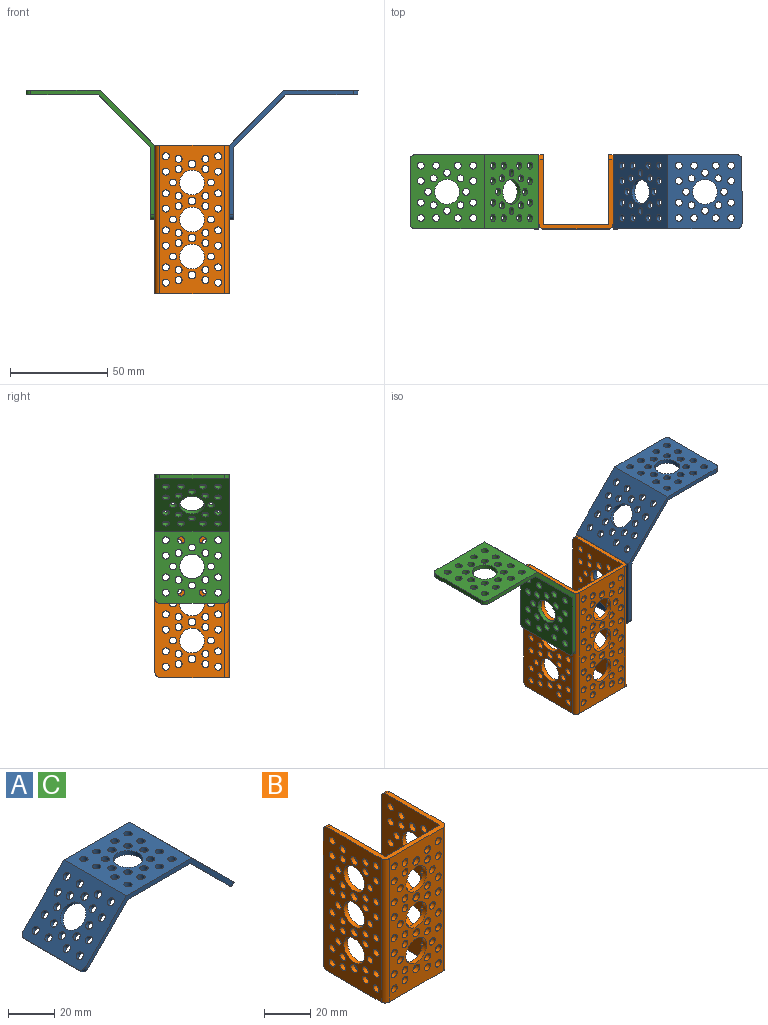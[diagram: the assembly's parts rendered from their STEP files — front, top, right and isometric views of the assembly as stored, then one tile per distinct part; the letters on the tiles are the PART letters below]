
ASSEMBLY  parts=3 mates=2
PART A: 77 faces, bbox 93.9x38.1x28.6 mm
  f0: cylinder r=1.78mm len=4.13mm, axis (-0.71,0,0.71), area 25.5mm2, adj f63,f69
  f1: cylinder r=1.78mm len=4.13mm, axis (-0.71,0,0.71), area 25.5mm2, adj f63,f69
  f2: cylinder r=1.78mm len=4.13mm, axis (-0.71,0,0.71), area 25.5mm2, adj f63,f69
  f3: cylinder r=1.78mm len=4.13mm, axis (-0.71,0,0.71), area 25.5mm2, adj f63,f69
  f4: cylinder r=1.78mm len=4.13mm, axis (-0.71,0,0.71), area 25.5mm2, adj f63,f69
  f5: cylinder r=1.78mm len=4.13mm, axis (-0.71,0,0.71), area 25.5mm2, adj f63,f69
  f6: cylinder r=1.78mm len=4.13mm, axis (-0.71,0,0.71), area 25.5mm2, adj f63,f69
  f7: cylinder r=1.78mm len=4.13mm, axis (-0.71,0,0.71), area 25.5mm2, adj f63,f69
  f8: cylinder r=1.78mm len=4.13mm, axis (0.71,0,0.71), area 25.5mm2, adj f64,f68
  f9: cylinder r=1.78mm len=4.13mm, axis (0.71,0,0.71), area 25.5mm2, adj f64,f68
  f10: cylinder r=1.78mm len=4.13mm, axis (0.71,0,0.71), area 25.5mm2, adj f64,f68
  f11: cylinder r=1.78mm len=4.13mm, axis (0.71,0,0.71), area 25.5mm2, adj f64,f68
  f12: cylinder r=1.78mm len=4.13mm, axis (0.71,0,0.71), area 25.5mm2, adj f64,f68
  f13: cylinder r=1.78mm len=4.13mm, axis (0.71,0,0.71), area 25.5mm2, adj f64,f68
  f14: cylinder r=1.78mm len=4.13mm, axis (0.71,0,0.71), area 25.5mm2, adj f64,f68
  f15: cylinder r=1.78mm len=4.13mm, axis (0.71,0,0.71), area 25.5mm2, adj f64,f68
  f16: cylinder r=1.78mm len=3.56mm, axis (0,0,-1), area 25.5mm2, adj f65,f66
  f17: cylinder r=1.78mm len=3.56mm, axis (0,0,-1), area 25.5mm2, adj f65,f66
  f18: cylinder r=1.78mm len=3.56mm, axis (0,0,-1), area 25.5mm2, adj f65,f66
  f19: cylinder r=1.78mm len=3.56mm, axis (0,0,-1), area 25.5mm2, adj f65,f66
  f20: cylinder r=1.78mm len=3.56mm, axis (0,0,-1), area 25.5mm2, adj f65,f66
  f21: cylinder r=1.78mm len=3.56mm, axis (0,0,-1), area 25.5mm2, adj f65,f66
  f22: cylinder r=1.78mm len=3.56mm, axis (0,0,-1), area 25.5mm2, adj f65,f66
  f23: cylinder r=1.78mm len=3.56mm, axis (0,0,-1), area 25.5mm2, adj f65,f66
  f24: cylinder r=1.78mm len=4.13mm, axis (-0.71,0,0.71), area 25.5mm2, adj f63,f69
  f25: cylinder r=1.78mm len=4.13mm, axis (-0.71,0,0.71), area 25.5mm2, adj f63,f69
  f26: cylinder r=1.78mm len=4.13mm, axis (-0.71,0,0.71), area 25.5mm2, adj f63,f69
  f27: cylinder r=1.78mm len=4.13mm, axis (-0.71,0,0.71), area 25.5mm2, adj f63,f69
  f28: cylinder r=1.78mm len=4.13mm, axis (0.71,0,0.71), area 25.5mm2, adj f64,f68
  f29: cylinder r=1.78mm len=4.13mm, axis (0.71,0,0.71), area 25.5mm2, adj f64,f68
  f30: cylinder r=1.78mm len=4.13mm, axis (0.71,0,0.71), area 25.5mm2, adj f64,f68
  f31: cylinder r=1.78mm len=4.13mm, axis (0.71,0,0.71), area 25.5mm2, adj f64,f68
  f32: cylinder r=1.78mm len=3.56mm, axis (0,0,-1), area 25.5mm2, adj f65,f66
  f33: cylinder r=1.78mm len=3.56mm, axis (0,0,-1), area 25.5mm2, adj f65,f66
  f34: cylinder r=1.78mm len=3.56mm, axis (0,0,-1), area 25.5mm2, adj f65,f66
  f35: cylinder r=1.78mm len=3.56mm, axis (0,0,-1), area 25.5mm2, adj f65,f66
  f36: cylinder r=1.78mm len=4.13mm, axis (0.71,0,0.71), area 25.5mm2, adj f64,f68
  f37: cylinder r=1.78mm len=4.13mm, axis (0.71,0,0.71), area 25.5mm2, adj f64,f68
  f38: cylinder r=1.78mm len=4.13mm, axis (0.71,0,0.71), area 25.5mm2, adj f64,f68
  f39: cylinder r=1.78mm len=4.13mm, axis (0.71,0,0.71), area 25.5mm2, adj f64,f68
  f40: cylinder r=1.78mm len=4.13mm, axis (0.71,0,0.71), area 25.5mm2, adj f64,f68
  f41: cylinder r=1.78mm len=4.13mm, axis (0.71,0,0.71), area 25.5mm2, adj f64,f68
  f42: cylinder r=1.78mm len=4.13mm, axis (0.71,0,0.71), area 25.5mm2, adj f64,f68
  f43: cylinder r=1.78mm len=4.13mm, axis (0.71,0,0.71), area 25.5mm2, adj f64,f68
  f44: cylinder r=1.78mm len=4.13mm, axis (-0.71,0,0.71), area 25.5mm2, adj f63,f69
  f45: cylinder r=1.78mm len=4.13mm, axis (-0.71,0,0.71), area 25.5mm2, adj f63,f69
  f46: cylinder r=1.78mm len=4.13mm, axis (-0.71,0,0.71), area 25.5mm2, adj f63,f69
  f47: cylinder r=1.78mm len=4.13mm, axis (-0.71,0,0.71), area 25.5mm2, adj f63,f69
  f48: cylinder r=1.78mm len=4.13mm, axis (-0.71,0,0.71), area 25.5mm2, adj f63,f69
  f49: cylinder r=1.78mm len=4.13mm, axis (-0.71,0,0.71), area 25.5mm2, adj f63,f69
  f50: cylinder r=1.78mm len=4.13mm, axis (-0.71,0,0.71), area 25.5mm2, adj f63,f69
  f51: cylinder r=1.78mm len=4.13mm, axis (-0.71,0,0.71), area 25.5mm2, adj f63,f69
  f52: cylinder r=1.78mm len=3.56mm, axis (0,0,1), area 25.5mm2, adj f65,f66
  f53: cylinder r=1.78mm len=3.56mm, axis (0,0,1), area 25.5mm2, adj f65,f66
  f54: cylinder r=1.78mm len=3.56mm, axis (0,0,1), area 25.5mm2, adj f65,f66
  f55: cylinder r=1.78mm len=3.56mm, axis (0,0,1), area 25.5mm2, adj f65,f66
  f56: cylinder r=1.78mm len=3.56mm, axis (0,0,1), area 25.5mm2, adj f65,f66
  f57: cylinder r=1.78mm len=3.56mm, axis (0,0,1), area 25.5mm2, adj f65,f66
  f58: cylinder r=1.78mm len=3.56mm, axis (0,0,1), area 25.5mm2, adj f65,f66
  f59: cylinder r=1.78mm len=3.56mm, axis (0,0,1), area 25.5mm2, adj f65,f66
  f60: cylinder r=6.36mm len=12.73mm, axis (-0.71,0,0.71), area 91.4mm2, adj f63,f69
  f61: cylinder r=6.36mm len=12.73mm, axis (0.71,0,0.71), area 91.4mm2, adj f64,f68
  f62: cylinder r=6.36mm len=12.73mm, axis (0,0,-1), area 91.4mm2, adj f65,f66
  f63: plane 38.1x26.94mm, normal (-0.71,0,0.71), area 1123mm2, adj f0,f1,f2,f3,f4,f5,f6,f7
  f64: plane 38.1x26.94mm, normal (0.71,0,0.71), area 1123mm2, adj f8,f9,f10,f11,f12,f13,f14,f15
  f65: plane 38.1x38.1mm, normal (0,0,-1), area 1125.8mm2, adj f16,f17,f18,f19,f20,f21,f22,f23
  f66: plane 39.99x38.1mm, normal (0,0,1), area 1197.9mm2, adj f16,f17,f18,f19,f20,f21,f22,f23
  f67: plane 33.02x1.62mm, normal (0.71,0,-0.71), area 75.5mm2, adj f64,f68,f75,f76
  f68: plane 38.1x26.27mm, normal (-0.71,0,-0.71), area 1087mm2, adj f8,f9,f10,f11,f12,f13,f14,f15
  f69: plane 38.1x26.27mm, normal (0.71,0,-0.71), area 1087mm2, adj f0,f1,f2,f3,f4,f5,f6,f7
  f70: plane 33.02x1.62mm, normal (-0.71,0,-0.71), area 75.5mm2, adj f63,f69,f73,f74
  f71: plane 90.28x26.76mm, normal (0,1,0), area 249.7mm2, adj f63,f64,f65,f66,f68,f69,f73,f75
  f72: plane 90.28x26.76mm, normal (0,-1,0), area 249.7mm2, adj f63,f64,f65,f66,f68,f69,f74,f76
  f73: cylinder r=2.54mm len=3.41mm, axis (0.71,0,-0.71), area 9.1mm2, adj f63,f69,f70,f71
  f74: cylinder r=2.54mm len=3.41mm, axis (-0.71,0,0.71), area 9.1mm2, adj f63,f69,f70,f72
  f75: cylinder r=2.54mm len=3.41mm, axis (0.71,0,0.71), area 9.1mm2, adj f64,f67,f68,f71
  f76: cylinder r=2.54mm len=3.41mm, axis (-0.71,0,-0.71), area 9.1mm2, adj f64,f67,f68,f72
PART B: 151 faces, bbox 38.1x38.1x76.2 mm
  f0: cylinder r=1.78mm len=3.56mm, axis (0,-1,0), area 25.5mm2, adj f135,f139
  f1: cylinder r=1.78mm len=3.56mm, axis (0,-1,0), area 25.5mm2, adj f135,f139
  f2: cylinder r=1.78mm len=3.56mm, axis (0,-1,0), area 25.5mm2, adj f135,f139
  f3: cylinder r=1.78mm len=3.56mm, axis (0,-1,0), area 25.5mm2, adj f135,f139
  f4: cylinder r=1.78mm len=3.56mm, axis (0,-1,0), area 25.5mm2, adj f135,f139
  f5: cylinder r=1.78mm len=3.56mm, axis (0,-1,0), area 25.5mm2, adj f135,f139
  f6: cylinder r=1.78mm len=3.56mm, axis (0,-1,0), area 25.5mm2, adj f135,f139
  f7: cylinder r=1.78mm len=3.56mm, axis (0,-1,0), area 25.5mm2, adj f135,f139
  f8: cylinder r=1.78mm len=3.56mm, axis (0,-1,0), area 25.5mm2, adj f135,f139
  f9: cylinder r=1.78mm len=3.56mm, axis (0,-1,0), area 25.5mm2, adj f135,f139
  f10: cylinder r=2.03mm len=4.06mm, axis (0,-1,0), area 29.2mm2, adj f135,f139
  f11: cylinder r=2.03mm len=4.06mm, axis (0,-1,0), area 29.2mm2, adj f135,f139
  f12: cylinder r=1.78mm len=3.56mm, axis (0,-1,0), area 25.5mm2, adj f135,f139
  f13: cylinder r=1.78mm len=3.56mm, axis (0,-1,0), area 25.5mm2, adj f135,f139
  f14: cylinder r=1.78mm len=3.56mm, axis (0,-1,0), area 25.5mm2, adj f135,f139
  f15: cylinder r=1.78mm len=3.56mm, axis (0,-1,0), area 25.5mm2, adj f135,f139
  f16: cylinder r=1.78mm len=3.56mm, axis (0,-1,0), area 25.5mm2, adj f135,f139
  f17: cylinder r=1.78mm len=3.56mm, axis (0,-1,0), area 25.5mm2, adj f135,f139
  f18: cylinder r=1.78mm len=3.56mm, axis (0,-1,0), area 25.5mm2, adj f135,f139
  f19: cylinder r=1.78mm len=3.56mm, axis (0,-1,0), area 25.5mm2, adj f135,f139
  f20: cylinder r=1.78mm len=3.56mm, axis (0,-1,0), area 25.5mm2, adj f135,f139
  f21: cylinder r=1.78mm len=3.56mm, axis (0,-1,0), area 25.5mm2, adj f135,f139
  f22: cylinder r=6.36mm len=12.73mm, axis (0,-1,0), area 91.4mm2, adj f135,f139
  f23: cylinder r=6.36mm len=12.73mm, axis (0,-1,0), area 91.4mm2, adj f135,f139
  f24: cylinder r=1.78mm len=3.56mm, axis (0,-1,0), area 25.5mm2, adj f135,f139
  f25: cylinder r=1.78mm len=3.56mm, axis (0,-1,0), area 25.5mm2, adj f135,f139
  f26: cylinder r=1.78mm len=3.56mm, axis (0,-1,0), area 25.5mm2, adj f135,f139
  f27: cylinder r=1.78mm len=3.56mm, axis (0,-1,0), area 25.5mm2, adj f135,f139
  f28: cylinder r=1.78mm len=3.56mm, axis (0,-1,0), area 25.5mm2, adj f135,f139
  f29: cylinder r=1.78mm len=3.56mm, axis (0,-1,0), area 25.5mm2, adj f135,f139
  f30: cylinder r=1.78mm len=3.56mm, axis (0,-1,0), area 25.5mm2, adj f135,f139
  f31: cylinder r=1.78mm len=3.56mm, axis (0,-1,0), area 25.5mm2, adj f135,f139
  f32: cylinder r=1.78mm len=3.56mm, axis (0,-1,0), area 25.5mm2, adj f135,f139
  f33: cylinder r=1.78mm len=3.56mm, axis (0,-1,0), area 25.5mm2, adj f135,f139
  f34: cylinder r=1.78mm len=3.56mm, axis (0,-1,0), area 25.5mm2, adj f135,f139
  f35: cylinder r=1.78mm len=3.56mm, axis (0,-1,0), area 25.5mm2, adj f135,f139
  f36: cylinder r=2.03mm len=4.06mm, axis (0,-1,0), area 29.2mm2, adj f135,f139
  f37: cylinder r=2.03mm len=4.06mm, axis (0,-1,0), area 29.2mm2, adj f135,f139
  f38: cylinder r=1.78mm len=3.56mm, axis (0,-1,0), area 25.5mm2, adj f135,f139
  f39: cylinder r=1.78mm len=3.56mm, axis (0,-1,0), area 25.5mm2, adj f135,f139
  f40: cylinder r=1.78mm len=3.56mm, axis (0,-1,0), area 25.5mm2, adj f135,f139
  f41: cylinder r=1.78mm len=3.56mm, axis (0,-1,0), area 25.5mm2, adj f135,f139
  f42: cylinder r=1.78mm len=3.56mm, axis (0,-1,0), area 25.5mm2, adj f135,f139
  f43: cylinder r=1.78mm len=3.56mm, axis (0,-1,0), area 25.5mm2, adj f135,f139
  f44: cylinder r=6.36mm len=12.73mm, axis (0,-1,0), area 91.4mm2, adj f135,f139
  f45: cylinder r=2.03mm len=4.06mm, axis (1,0,0), area 29.2mm2, adj f136,f138
  f46: cylinder r=2.03mm len=4.06mm, axis (1,0,0), area 29.2mm2, adj f140,f142
  f47: cylinder r=1.78mm len=3.56mm, axis (1,0,0), area 25.5mm2, adj f136,f138
  f48: cylinder r=1.78mm len=3.56mm, axis (1,0,0), area 25.5mm2, adj f140,f142
  f49: cylinder r=1.78mm len=3.56mm, axis (1,0,0), area 25.5mm2, adj f136,f138
  f50: cylinder r=1.78mm len=3.56mm, axis (1,0,0), area 25.5mm2, adj f140,f142
  f51: cylinder r=1.78mm len=3.56mm, axis (1,0,0), area 25.5mm2, adj f136,f138
  f52: cylinder r=1.78mm len=3.56mm, axis (1,0,0), area 25.5mm2, adj f140,f142
  f53: cylinder r=1.78mm len=3.56mm, axis (1,0,0), area 25.5mm2, adj f136,f138
  f54: cylinder r=1.78mm len=3.56mm, axis (1,0,0), area 25.5mm2, adj f140,f142
  f55: cylinder r=1.78mm len=3.56mm, axis (1,0,0), area 25.5mm2, adj f136,f138
  f56: cylinder r=1.78mm len=3.56mm, axis (1,0,0), area 25.5mm2, adj f140,f142
  f57: cylinder r=1.78mm len=3.56mm, axis (1,0,0), area 25.5mm2, adj f136,f138
  f58: cylinder r=1.78mm len=3.56mm, axis (1,0,0), area 25.5mm2, adj f140,f142
  f59: cylinder r=1.78mm len=3.56mm, axis (1,0,0), area 25.5mm2, adj f136,f138
  f60: cylinder r=1.78mm len=3.56mm, axis (1,0,0), area 25.5mm2, adj f140,f142
  f61: cylinder r=1.78mm len=3.56mm, axis (1,0,0), area 25.5mm2, adj f136,f138
  f62: cylinder r=1.78mm len=3.56mm, axis (1,0,0), area 25.5mm2, adj f140,f142
  f63: cylinder r=1.78mm len=3.56mm, axis (1,0,0), area 25.5mm2, adj f136,f138
  f64: cylinder r=1.78mm len=3.56mm, axis (1,0,0), area 25.5mm2, adj f140,f142
  f65: cylinder r=1.78mm len=3.56mm, axis (1,0,0), area 25.5mm2, adj f136,f138
  f66: cylinder r=1.78mm len=3.56mm, axis (1,0,0), area 25.5mm2, adj f140,f142
  f67: cylinder r=1.78mm len=3.56mm, axis (1,0,0), area 25.5mm2, adj f136,f138
  f68: cylinder r=1.78mm len=3.56mm, axis (1,0,0), area 25.5mm2, adj f140,f142
  f69: cylinder r=1.78mm len=3.56mm, axis (1,0,0), area 25.5mm2, adj f136,f138
  f70: cylinder r=1.78mm len=3.56mm, axis (1,0,0), area 25.5mm2, adj f140,f142
  f71: cylinder r=1.78mm len=3.56mm, axis (1,0,0), area 25.5mm2, adj f136,f138
  f72: cylinder r=1.78mm len=3.56mm, axis (1,0,0), area 25.5mm2, adj f140,f142
  f73: cylinder r=1.78mm len=3.56mm, axis (1,0,0), area 25.5mm2, adj f136,f138
  f74: cylinder r=1.78mm len=3.56mm, axis (1,0,0), area 25.5mm2, adj f140,f142
  f75: cylinder r=1.78mm len=3.56mm, axis (1,0,0), area 25.5mm2, adj f136,f138
  f76: cylinder r=1.78mm len=3.56mm, axis (1,0,0), area 25.5mm2, adj f140,f142
  f77: cylinder r=1.78mm len=3.56mm, axis (1,0,0), area 25.5mm2, adj f136,f138
  f78: cylinder r=1.78mm len=3.56mm, axis (1,0,0), area 25.5mm2, adj f140,f142
  f79: cylinder r=2.03mm len=4.06mm, axis (1,0,0), area 29.2mm2, adj f136,f138
  f80: cylinder r=2.03mm len=4.06mm, axis (1,0,0), area 29.2mm2, adj f140,f142
  f81: cylinder r=1.78mm len=3.56mm, axis (1,0,0), area 25.5mm2, adj f136,f138
  f82: cylinder r=1.78mm len=3.56mm, axis (1,0,0), area 25.5mm2, adj f140,f142
  f83: cylinder r=1.78mm len=3.56mm, axis (1,0,0), area 25.5mm2, adj f136,f138
  f84: cylinder r=1.78mm len=3.56mm, axis (1,0,0), area 25.5mm2, adj f140,f142
  f85: cylinder r=1.78mm len=3.56mm, axis (1,0,0), area 25.5mm2, adj f136,f138
  f86: cylinder r=1.78mm len=3.56mm, axis (1,0,0), area 25.5mm2, adj f140,f142
  f87: cylinder r=1.78mm len=3.56mm, axis (1,0,0), area 25.5mm2, adj f136,f138
  f88: cylinder r=1.78mm len=3.56mm, axis (1,0,0), area 25.5mm2, adj f140,f142
  f89: cylinder r=1.78mm len=3.56mm, axis (1,0,0), area 25.5mm2, adj f136,f138
  f90: cylinder r=1.78mm len=3.56mm, axis (1,0,0), area 25.5mm2, adj f140,f142
  f91: cylinder r=1.78mm len=3.56mm, axis (1,0,0), area 25.5mm2, adj f136,f138
  f92: cylinder r=1.78mm len=3.56mm, axis (1,0,0), area 25.5mm2, adj f140,f142
  f93: cylinder r=1.78mm len=3.56mm, axis (1,0,0), area 25.5mm2, adj f136,f138
  f94: cylinder r=1.78mm len=3.56mm, axis (1,0,0), area 25.5mm2, adj f140,f142
  f95: cylinder r=1.78mm len=3.56mm, axis (1,0,0), area 25.5mm2, adj f136,f138
  f96: cylinder r=1.78mm len=3.56mm, axis (1,0,0), area 25.5mm2, adj f140,f142
  f97: cylinder r=1.78mm len=3.56mm, axis (1,0,0), area 25.5mm2, adj f136,f138
  f98: cylinder r=1.78mm len=3.56mm, axis (1,0,0), area 25.5mm2, adj f140,f142
  f99: cylinder r=1.78mm len=3.56mm, axis (1,0,0), area 25.5mm2, adj f136,f138
  f100: cylinder r=1.78mm len=3.56mm, axis (1,0,0), area 25.5mm2, adj f140,f142
  f101: cylinder r=1.78mm len=3.56mm, axis (1,0,0), area 25.5mm2, adj f136,f138
  f102: cylinder r=1.78mm len=3.56mm, axis (1,0,0), area 25.5mm2, adj f140,f142
  f103: cylinder r=1.78mm len=3.56mm, axis (1,0,0), area 25.5mm2, adj f136,f138
  f104: cylinder r=1.78mm len=3.56mm, axis (1,0,0), area 25.5mm2, adj f140,f142
  f105: cylinder r=6.36mm len=12.73mm, axis (1,0,0), area 91.4mm2, adj f140,f142
  f106: cylinder r=6.36mm len=12.73mm, axis (1,0,0), area 91.4mm2, adj f140,f142
  f107: cylinder r=6.36mm len=12.73mm, axis (1,0,0), area 91.4mm2, adj f136,f138
  f108: cylinder r=6.36mm len=12.73mm, axis (1,0,0), area 91.4mm2, adj f136,f138
  f109: cylinder r=1.78mm len=3.56mm, axis (1,0,0), area 25.5mm2, adj f136,f138
  f110: cylinder r=1.78mm len=3.56mm, axis (1,0,0), area 25.5mm2, adj f140,f142
  f111: cylinder r=1.78mm len=3.56mm, axis (1,0,0), area 25.5mm2, adj f136,f138
  f112: cylinder r=1.78mm len=3.56mm, axis (1,0,0), area 25.5mm2, adj f140,f142
  f113: cylinder r=1.78mm len=3.56mm, axis (1,0,0), area 25.5mm2, adj f136,f138
  f114: cylinder r=1.78mm len=3.56mm, axis (1,0,0), area 25.5mm2, adj f140,f142
  f115: cylinder r=1.78mm len=3.56mm, axis (1,0,0), area 25.5mm2, adj f136,f138
  f116: cylinder r=1.78mm len=3.56mm, axis (1,0,0), area 25.5mm2, adj f140,f142
  f117: cylinder r=2.03mm len=4.06mm, axis (1,0,0), area 29.2mm2, adj f136,f138
  f118: cylinder r=2.03mm len=4.06mm, axis (1,0,0), area 29.2mm2, adj f140,f142
  f119: cylinder r=2.03mm len=4.06mm, axis (1,0,0), area 29.2mm2, adj f136,f138
  f120: cylinder r=2.03mm len=4.06mm, axis (1,0,0), area 29.2mm2, adj f140,f142
  f121: cylinder r=1.78mm len=3.56mm, axis (1,0,0), area 25.5mm2, adj f136,f138
  f122: cylinder r=1.78mm len=3.56mm, axis (1,0,0), area 25.5mm2, adj f140,f142
  f123: cylinder r=1.78mm len=3.56mm, axis (1,0,0), area 25.5mm2, adj f136,f138
  f124: cylinder r=1.78mm len=3.56mm, axis (1,0,0), area 25.5mm2, adj f140,f142
  f125: cylinder r=1.78mm len=3.56mm, axis (1,0,0), area 25.5mm2, adj f136,f138
  f126: cylinder r=1.78mm len=3.56mm, axis (1,0,0), area 25.5mm2, adj f140,f142
  f127: cylinder r=1.78mm len=3.56mm, axis (1,0,0), area 25.5mm2, adj f136,f138
  f128: cylinder r=1.78mm len=3.56mm, axis (1,0,0), area 25.5mm2, adj f140,f142
  f129: cylinder r=1.78mm len=3.56mm, axis (1,0,0), area 25.5mm2, adj f136,f138
  f130: cylinder r=1.78mm len=3.56mm, axis (1,0,0), area 25.5mm2, adj f140,f142
  f131: cylinder r=1.78mm len=3.56mm, axis (1,0,0), area 25.5mm2, adj f136,f138
  f132: cylinder r=1.78mm len=3.56mm, axis (1,0,0), area 25.5mm2, adj f140,f142
  f133: cylinder r=6.36mm len=12.73mm, axis (1,0,0), area 91.4mm2, adj f136,f138
  f134: cylinder r=6.36mm len=12.73mm, axis (1,0,0), area 91.4mm2, adj f140,f142
  f135: plane 76.2x33.02mm, normal (0,-1,0), area 1705.3mm2, adj f0,f1,f2,f3,f4,f5,f6,f7
  f136: plane 76.2x35.56mm, normal (1,0,0), area 1896.1mm2, adj f45,f47,f49,f51,f53,f55,f57,f59
  f137: plane 71.12x2.29mm, normal (0,1,0), area 162.6mm2, adj f136,f138,f146,f150
  f138: plane 76.2x35.81mm, normal (-1,0,0), area 1915.4mm2, adj f45,f47,f49,f51,f53,f55,f57,f59
  f139: plane 76.2x33.53mm, normal (0,1,0), area 1744mm2, adj f0,f1,f2,f3,f4,f5,f6,f7
  f140: plane 76.2x35.81mm, normal (1,0,0), area 1915.4mm2, adj f46,f48,f50,f52,f54,f56,f58,f60
  f141: plane 71.12x2.29mm, normal (0,1,0), area 162.6mm2, adj f140,f142,f145,f149
  f142: plane 76.2x35.56mm, normal (-1,0,0), area 1896.1mm2, adj f46,f48,f50,f52,f54,f56,f58,f60
  f143: plane 38.1x35.56mm, normal (0,0,1), area 236.5mm2, adj f135,f136,f138,f139,f140,f142,f145,f146
  f144: plane 38.1x35.56mm, normal (0,0,-1), area 236.5mm2, adj f135,f136,f138,f139,f140,f142,f147,f148
  f145: cylinder r=2.54mm len=2.54mm, axis (-1,0,0), area 9.1mm2, adj f140,f141,f142,f143
  f146: cylinder r=2.54mm len=2.54mm, axis (-1,0,0), area 9.1mm2, adj f136,f137,f138,f143
  f147: cylinder r=2.54mm len=76.2mm, axis (0,0,-1), area 304mm2, adj f135,f142,f143,f144
  f148: cylinder r=2.54mm len=76.2mm, axis (0,0,-1), area 304mm2, adj f135,f136,f143,f144
  f149: cylinder r=2.54mm len=2.54mm, axis (1,0,0), area 9.1mm2, adj f140,f141,f142,f144
  f150: cylinder r=2.54mm len=2.54mm, axis (1,0,0), area 9.1mm2, adj f136,f137,f138,f144
PART C: same geometry as A
PLACE A rot(axis=(0,-1,0),45deg) t=(46.11,9.01,83.14)mm
PLACE B t=(-6.13,9.01,-7.2)mm
PLACE C rot(axis=(0,1,0),45deg) t=(-20.27,9.01,83.14)mm
MATE fastened A.f51 <-> B.f89  axis (-1,0,0) through (31.97,37.84,49.95)mm
MATE fastened C.f43 <-> B.f89  axis (1,0,0) through (-6.13,37.84,49.95)mm
